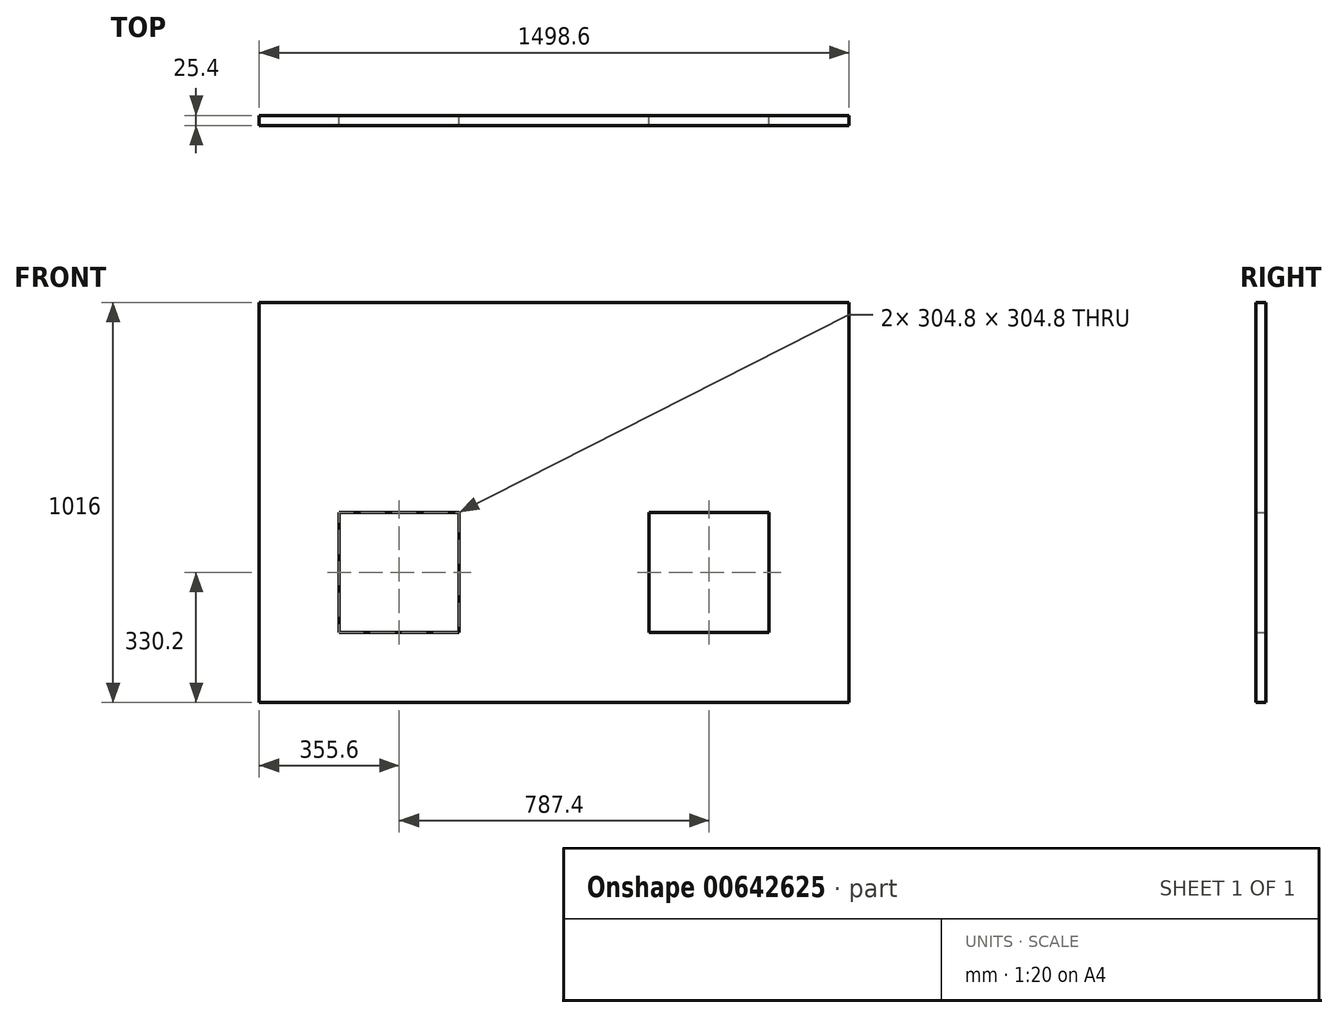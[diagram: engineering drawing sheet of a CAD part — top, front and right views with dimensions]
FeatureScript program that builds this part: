
annotation { "Feature Type Name" : "Feature", "Feature Type Description" : "" }
export const myFeature = defineFeature(function(context is Context, id is Id, definition is map)
    precondition{}
    {
        {
            var Q0;
            Q0=qCreatedBy(makeId("Front.planeOp"),FACE);
            var sketch = newSketch(context, id + "F0", { "sketchPlane" : qUnion([Q0])});
            skLineSegment(sketch, "E0.bottom", {"start": v(-749.3, 0) * mm, "end": v(749.3, 0) * mm});
            skLineSegment(sketch, "E0.top", {"start": v(-749.3, 1016) * mm, "end": v(749.3, 1016) * mm});
            skLineSegment(sketch, "E0.left", {"start": v(-749.3, 0) * mm, "end": v(-749.3, 1016) * mm});
            skLineSegment(sketch, "E0.right", {"start": v(749.3, 0) * mm, "end": v(749.3, 1016) * mm});
            skLineSegment(sketch, "E1.bottom", {"start": v(-546.1, 482.6) * mm, "end": v(-241.3, 482.6) * mm});
            skLineSegment(sketch, "E1.top", {"start": v(-546.1, 177.8) * mm, "end": v(-241.3, 177.8) * mm});
            skLineSegment(sketch, "E1.left", {"start": v(-546.1, 482.6) * mm, "end": v(-546.1, 177.8) * mm});
            skLineSegment(sketch, "E1.right", {"start": v(-241.3, 482.6) * mm, "end": v(-241.3, 177.8) * mm});
            skLineSegment(sketch, "E2.bottom", {"start": v(241.3, 482.6) * mm, "end": v(546.1, 482.6) * mm});
            skLineSegment(sketch, "E2.top", {"start": v(241.3, 177.8) * mm, "end": v(546.1, 177.8) * mm});
            skLineSegment(sketch, "E2.left", {"start": v(241.3, 482.6) * mm, "end": v(241.3, 177.8) * mm});
            skLineSegment(sketch, "E2.right", {"start": v(546.1, 482.6) * mm, "end": v(546.1, 177.8) * mm});
            skSolve(sketch);
        }
        {
            var Q0;
            Q0=makeQuery(id+"F0.imprint","IMPRINT",FACE,{"disambiguationData":[TD([[makeQuery(id+"F0.imprint","IMPRINT",EDGE,{"derivedFrom":sQuery(id+"F0.wireOp",EDGE,"E0.bottom")}),1.0]])]});
            extrude(context, id + "F1", {"entities" : qUnion([Q0]), "depth" : 25.4 * mm, "offsetDistance" : 25 * mm});
        }
    });
